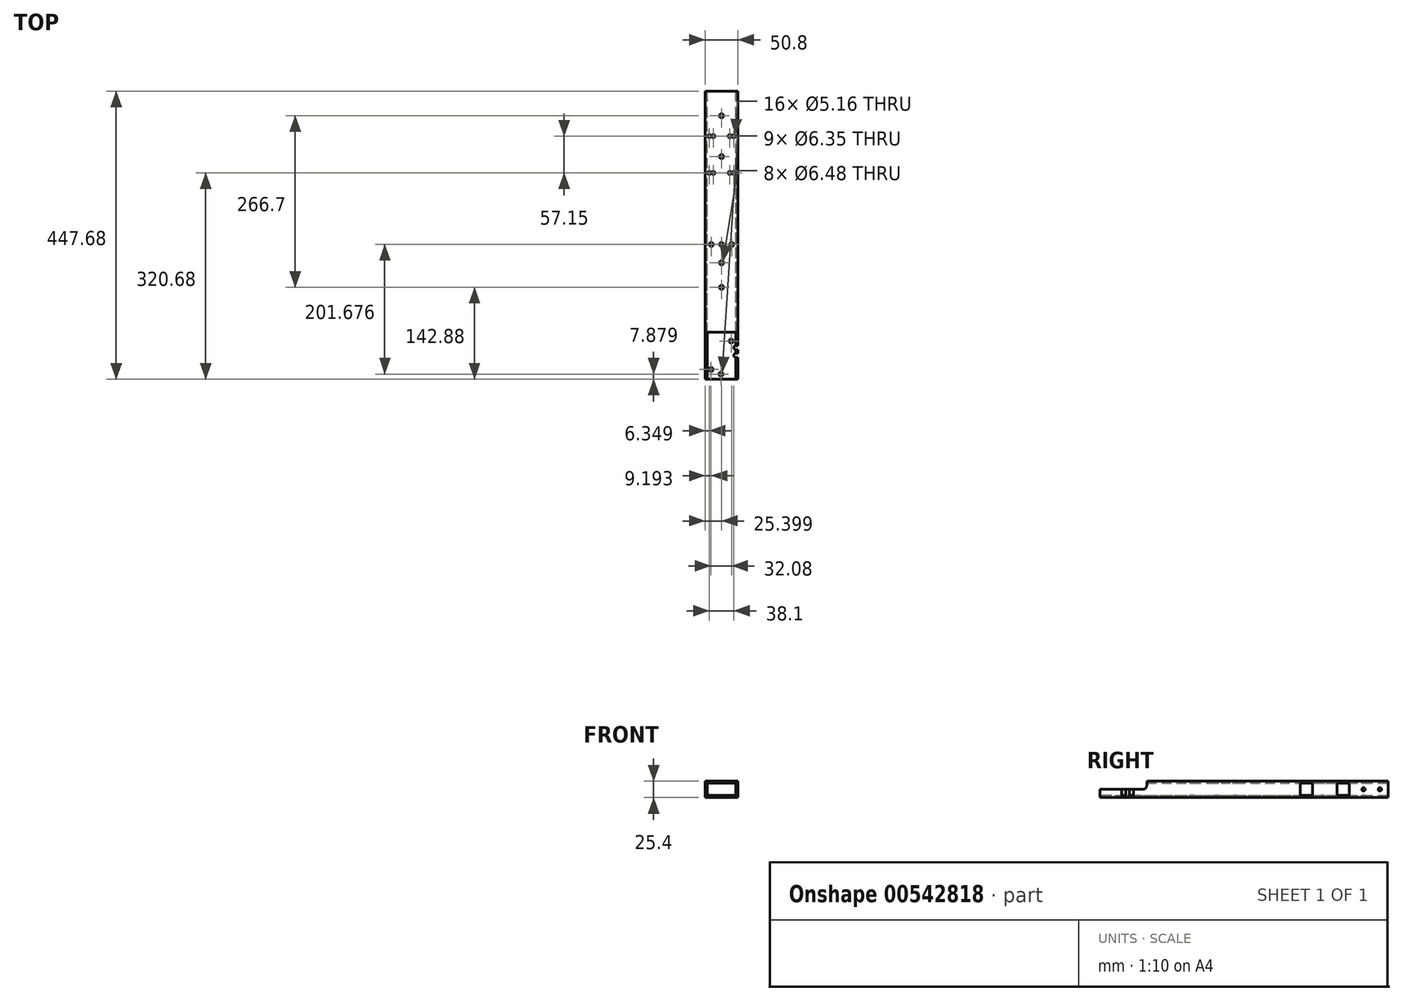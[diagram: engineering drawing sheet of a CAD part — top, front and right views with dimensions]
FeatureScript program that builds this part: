
annotation { "Feature Type Name" : "Feature", "Feature Type Description" : "" }
export const myFeature = defineFeature(function(context is Context, id is Id, definition is map)
    precondition{}
    {
        {
            var Q0;
            Q0=qCreatedBy(makeId("Front.planeOp"),FACE);
            var sketch = newSketch(context, id + "F0", { "sketchPlane" : qUnion([Q0])});
            skLineSegment(sketch, "E0.bottom", {"start": v(-52.6, 29.87) * mm, "end": v(-1.8, 29.87) * mm});
            skLineSegment(sketch, "E0.top", {"start": v(-52.6, 4.47) * mm, "end": v(-1.8, 4.47) * mm});
            skLineSegment(sketch, "E0.left", {"start": v(-52.6, 29.87) * mm, "end": v(-52.6, 4.47) * mm});
            skLineSegment(sketch, "E0.right", {"start": v(-1.8, 29.87) * mm, "end": v(-1.8, 4.47) * mm});
            skLineSegment(sketch, "E1.bottom", {"start": v(-49.43, 26.7) * mm, "end": v(-4.98, 26.7) * mm});
            skLineSegment(sketch, "E1.top", {"start": v(-49.43, 7.65) * mm, "end": v(-4.98, 7.65) * mm});
            skLineSegment(sketch, "E1.left", {"start": v(-49.43, 26.7) * mm, "end": v(-49.43, 7.65) * mm});
            skLineSegment(sketch, "E1.right", {"start": v(-4.98, 26.7) * mm, "end": v(-4.98, 7.65) * mm});
            skSolve(sketch);
        }
        {
            var Q0;
            Q0=makeQuery(id+"F0.imprint","IMPRINT",FACE,{"disambiguationData":[TD([[makeQuery(id+"F0.imprint","IMPRINT",EDGE,{"derivedFrom":sQuery(id+"F0.wireOp",EDGE,"E0.bottom")}),-1.0]])]});
            extrude(context, id + "F1", {"entities" : qUnion([Q0]), "depth" : 447.67 * mm, "offsetDistance" : 25.4 * mm});
        }
        {
            var Q0;
            Q0=makeQuery(id+"F1.opExtrude","SWEPT_FACE",FACE,{"disambiguationData":[OSD([sQuery(id+"F0.wireOp",EDGE,"E0.bottom")])]});
            var sketch = newSketch(context, id + "F2", { "sketchPlane" : qUnion([Q0])});
            skCircle(sketch, "E2", {"center": v(-27.2, -38.1) * mm, "radius": 3.24 * mm});
            skPoint(sketch, "E2.centerSnap0", {"position": v(-27.2, 0) * mm});
            skCircle(sketch, "E3", {"center": v(-27.2, -101.6) * mm, "radius": 3.24 * mm});
            skCircle(sketch, "E4", {"center": v(-27.2, -266.7) * mm, "radius": 3.24 * mm});
            skCircle(sketch, "E5", {"center": v(-27.2, -304.8) * mm, "radius": 3.24 * mm});
            skCircle(sketch, "E6", {"center": v(-46.25, -127) * mm, "radius": 2.58 * mm});
            skCircle(sketch, "E7", {"center": v(-39.9, -127) * mm, "radius": 2.58 * mm});
            skCircle(sketch, "E8", {"center": v(-14.5, -127) * mm, "radius": 2.58 * mm});
            skCircle(sketch, "E9", {"center": v(-8.15, -127) * mm, "radius": 2.58 * mm});
            skCircle(sketch, "E10", {"center": v(-46.25, -69.85) * mm, "radius": 2.58 * mm});
            skCircle(sketch, "E11", {"center": v(-39.9, -69.85) * mm, "radius": 2.58 * mm});
            skCircle(sketch, "E12", {"center": v(-14.5, -69.85) * mm, "radius": 2.58 * mm});
            skCircle(sketch, "E13", {"center": v(-8.15, -69.85) * mm, "radius": 2.58 * mm});
            skCircle(sketch, "E14", {"center": v(-43.08, -238.13) * mm, "radius": 3.18 * mm});
            skCircle(sketch, "E15", {"center": v(-27.2, -238.13) * mm, "radius": 3.18 * mm});
            skCircle(sketch, "E16", {"center": v(-11.33, -238.13) * mm, "radius": 3.18 * mm});
            skCircle(sketch, "E17", {"center": v(-12.09, -388.37) * mm, "radius": 3.18 * mm});
            skCircle(sketch, "E18", {"center": v(-27.96, -439.8) * mm, "radius": 3.18 * mm});
            skCircle(sketch, "E19", {"center": v(-43.4, -432.54) * mm, "radius": 3.18 * mm});
            skArc(sketch, "E20", {"start": v(-4.98, -407.54) * mm, "mid": v(-8.15, -410.72) * mm, "end": v(-4.98, -413.9) * mm});
            skArc(sketch, "E21", {"start": v(-4.98, -395.35) * mm, "mid": v(-8.15, -398.53) * mm, "end": v(-4.98, -401.7) * mm});
            skLineSegment(sketch, "E22", {"start": v(-4.98, -413.9) * mm, "end": v(-1.8, -413.9) * mm});
            skLineSegment(sketch, "E23", {"start": v(-4.98, -407.54) * mm, "end": v(-1.8, -407.54) * mm});
            skLineSegment(sketch, "E24", {"start": v(-4.98, -401.7) * mm, "end": v(-1.8, -401.7) * mm});
            skLineSegment(sketch, "E25", {"start": v(-4.98, -395.35) * mm, "end": v(-1.8, -395.35) * mm});
            skSolve(sketch);
        }
        {
            var Q0;
            Q0=makeQuery(id+"F2.imprint","IMPRINT",FACE,{"disambiguationData":[TD([[makeQuery(id+"F2.imprint","IMPRINT",EDGE,{"derivedFrom":sQuery(id+"F2.wireOp",EDGE,"E5")}),1.0]])]});
            var Q1;
            Q1=makeQuery(id+"F2.imprint","IMPRINT",FACE,{"disambiguationData":[TD([[makeQuery(id+"F2.imprint","IMPRINT",EDGE,{"derivedFrom":sQuery(id+"F2.wireOp",EDGE,"E4")}),1.0]])]});
            var Q2;
            Q2=makeQuery(id+"F2.imprint","IMPRINT",FACE,{"disambiguationData":[TD([[makeQuery(id+"F2.imprint","IMPRINT",EDGE,{"derivedFrom":sQuery(id+"F2.wireOp",EDGE,"E3")}),1.0]])]});
            var Q3;
            Q3=makeQuery(id+"F2.imprint","IMPRINT",FACE,{"disambiguationData":[TD([[makeQuery(id+"F2.imprint","IMPRINT",EDGE,{"derivedFrom":sQuery(id+"F2.wireOp",EDGE,"E2")}),1.0]])]});
            var Q4;
            Q4=makeQuery(id+"F2.imprint","IMPRINT",FACE,{"disambiguationData":[TD([[makeQuery(id+"F2.imprint","IMPRINT",EDGE,{"derivedFrom":sQuery(id+"F2.wireOp",EDGE,"E6")}),1.0]])]});
            var Q5;
            Q5=makeQuery(id+"F2.imprint","IMPRINT",FACE,{"disambiguationData":[TD([[makeQuery(id+"F2.imprint","IMPRINT",EDGE,{"derivedFrom":sQuery(id+"F2.wireOp",EDGE,"E7")}),1.0]])]});
            var Q6;
            Q6=makeQuery(id+"F2.imprint","IMPRINT",FACE,{"disambiguationData":[TD([[makeQuery(id+"F2.imprint","IMPRINT",EDGE,{"derivedFrom":sQuery(id+"F2.wireOp",EDGE,"E8")}),1.0]])]});
            var Q7;
            Q7=makeQuery(id+"F2.imprint","IMPRINT",FACE,{"disambiguationData":[TD([[makeQuery(id+"F2.imprint","IMPRINT",EDGE,{"derivedFrom":sQuery(id+"F2.wireOp",EDGE,"E9")}),1.0]])]});
            var Q8;
            Q8=makeQuery(id+"F2.imprint","IMPRINT",FACE,{"disambiguationData":[TD([[makeQuery(id+"F2.imprint","IMPRINT",EDGE,{"derivedFrom":sQuery(id+"F2.wireOp",EDGE,"E10")}),1.0]])]});
            var Q9;
            Q9=makeQuery(id+"F2.imprint","IMPRINT",FACE,{"disambiguationData":[TD([[makeQuery(id+"F2.imprint","IMPRINT",EDGE,{"derivedFrom":sQuery(id+"F2.wireOp",EDGE,"E11")}),1.0]])]});
            var Q10;
            Q10=makeQuery(id+"F2.imprint","IMPRINT",FACE,{"disambiguationData":[TD([[makeQuery(id+"F2.imprint","IMPRINT",EDGE,{"derivedFrom":sQuery(id+"F2.wireOp",EDGE,"E12")}),1.0]])]});
            var Q11;
            Q11=makeQuery(id+"F2.imprint","IMPRINT",FACE,{"disambiguationData":[TD([[makeQuery(id+"F2.imprint","IMPRINT",EDGE,{"derivedFrom":sQuery(id+"F2.wireOp",EDGE,"E13")}),1.0]])]});
            var Q12;
            Q12=makeQuery(id+"F2.imprint","IMPRINT",FACE,{"disambiguationData":[TD([[makeQuery(id+"F2.imprint","IMPRINT",EDGE,{"derivedFrom":sQuery(id+"F2.wireOp",EDGE,"E14")}),1.0]])]});
            var Q13;
            Q13=makeQuery(id+"F2.imprint","IMPRINT",FACE,{"disambiguationData":[TD([[makeQuery(id+"F2.imprint","IMPRINT",EDGE,{"derivedFrom":sQuery(id+"F2.wireOp",EDGE,"E15")}),1.0]])]});
            var Q14;
            Q14=makeQuery(id+"F2.imprint","IMPRINT",FACE,{"disambiguationData":[TD([[makeQuery(id+"F2.imprint","IMPRINT",EDGE,{"derivedFrom":sQuery(id+"F2.wireOp",EDGE,"E16")}),1.0]])]});
            var Q15;
            Q15=makeQuery(id+"F2.imprint","IMPRINT",FACE,{"disambiguationData":[TD([[makeQuery(id+"F2.imprint","IMPRINT",EDGE,{"derivedFrom":sQuery(id+"F2.wireOp",EDGE,"E17")}),1.0]])]});
            extrude(context, id + "F3", {"entities" : qUnion([Q0, Q1, Q2, Q3, Q4, Q5, Q6, Q7, Q8, Q9, Q10, Q11, Q12, Q13, Q14, Q15]), "operationType" : NewBodyOperationType.REMOVE, "oppositeDirection" : true, "depth" : 25.4 * mm, "offsetDistance" : 25.4 * mm});
        }
        {
            var Q0;
            Q0=makeQuery(id+"F1.opExtrude","SWEPT_FACE",FACE,{"disambiguationData":[OSD([sQuery(id+"F0.wireOp",EDGE,"E0.left")])]});
            var sketch = newSketch(context, id + "F4", { "sketchPlane" : qUnion([Q0])});
            skCircle(sketch, "E26", {"center": v(12.7, 17.17) * mm, "radius": 2.58 * mm});
            skPoint(sketch, "E26.centerSnap0", {"position": v(0, 17.17) * mm});
            skCircle(sketch, "E27", {"center": v(38.1, 17.17) * mm, "radius": 2.58 * mm});
            skLineSegment(sketch, "E28.bottom", {"start": v(61.93, 7.65) * mm, "end": v(77.77, 7.65) * mm});
            skLineSegment(sketch, "E28.top", {"start": v(61.93, 26.7) * mm, "end": v(77.77, 26.7) * mm});
            skLineSegment(sketch, "E28.left", {"start": v(60.33, 9.25) * mm, "end": v(60.33, 25.1) * mm});
            skLineSegment(sketch, "E28.right", {"start": v(79.38, 9.25) * mm, "end": v(79.38, 25.1) * mm});
            skArc(sketch, "E29", {"start": v(61.93, 7.65) * mm, "mid": v(60.8, 8.12) * mm, "end": v(60.33, 9.25) * mm});
            skArc(sketch, "E30", {"start": v(60.33, 25.1) * mm, "mid": v(60.8, 26.23) * mm, "end": v(61.93, 26.7) * mm});
            skArc(sketch, "E31", {"start": v(77.77, 26.7) * mm, "mid": v(78.9, 26.23) * mm, "end": v(79.38, 25.1) * mm});
            skArc(sketch, "E32", {"start": v(79.38, 9.25) * mm, "mid": v(78.9, 8.12) * mm, "end": v(77.77, 7.65) * mm});
            skLineSegment(sketch, "E33.bottom", {"start": v(119.08, 7.65) * mm, "end": v(134.92, 7.65) * mm});
            skLineSegment(sketch, "E33.top", {"start": v(119.08, 26.7) * mm, "end": v(134.92, 26.7) * mm});
            skLineSegment(sketch, "E33.left", {"start": v(117.47, 9.25) * mm, "end": v(117.47, 25.1) * mm});
            skLineSegment(sketch, "E33.right", {"start": v(136.53, 9.25) * mm, "end": v(136.53, 25.1) * mm});
            skArc(sketch, "E34", {"start": v(119.08, 7.65) * mm, "mid": v(117.94, 8.12) * mm, "end": v(117.47, 9.25) * mm});
            skArc(sketch, "E35", {"start": v(117.47, 25.1) * mm, "mid": v(117.94, 26.23) * mm, "end": v(119.08, 26.7) * mm});
            skArc(sketch, "E36", {"start": v(134.92, 26.7) * mm, "mid": v(136.06, 26.23) * mm, "end": v(136.53, 25.1) * mm});
            skArc(sketch, "E37", {"start": v(136.53, 9.25) * mm, "mid": v(136.06, 8.12) * mm, "end": v(134.92, 7.65) * mm});
            skLineSegment(sketch, "E38.bottom", {"start": v(381, 17.17) * mm, "end": v(447.68, 17.17) * mm});
            skLineSegment(sketch, "E38.top", {"start": v(374.65, 29.87) * mm, "end": v(447.68, 29.87) * mm});
            skLineSegment(sketch, "E38.left", {"start": v(374.65, 23.52) * mm, "end": v(374.65, 29.87) * mm});
            skLineSegment(sketch, "E38.right", {"start": v(447.68, 17.17) * mm, "end": v(447.68, 29.87) * mm});
            skArc(sketch, "E39", {"start": v(381, 17.17) * mm, "mid": v(376.5, 19.03) * mm, "end": v(374.65, 23.52) * mm});
            skSolve(sketch);
        }
        {
            var Q0;
            Q0=makeQuery(id+"F4.imprint","IMPRINT",FACE,{"disambiguationData":[TD([[makeQuery(id+"F4.imprint","IMPRINT",EDGE,{"derivedFrom":sQuery(id+"F4.wireOp",EDGE,"E27")}),1.0]])]});
            var Q1;
            Q1=makeQuery(id+"F4.imprint","IMPRINT",FACE,{"disambiguationData":[TD([[makeQuery(id+"F4.imprint","IMPRINT",EDGE,{"derivedFrom":sQuery(id+"F4.wireOp",EDGE,"E26")}),1.0]])]});
            var Q2;
            Q2=makeQuery(id+"F4.imprint","IMPRINT",FACE,{"disambiguationData":[TD([[makeQuery(id+"F4.imprint","IMPRINT",EDGE,{"derivedFrom":sQuery(id+"F4.wireOp",EDGE,"E28.bottom")}),1.0]])]});
            var Q3;
            Q3=makeQuery(id+"F4.imprint","IMPRINT",FACE,{"disambiguationData":[TD([[makeQuery(id+"F4.imprint","IMPRINT",EDGE,{"derivedFrom":sQuery(id+"F4.wireOp",EDGE,"E33.bottom")}),1.0]])]});
            extrude(context, id + "F5", {"entities" : qUnion([Q0, Q1, Q2, Q3]), "operationType" : NewBodyOperationType.REMOVE, "endBound" : BoundingType.THROUGH_ALL, "oppositeDirection" : true, "depth" : 25.4 * mm, "offsetDistance" : 25.4 * mm});
        }
        {
            var Q0;
            Q0=qSketchRegion(id+"F4",true);
            extrude(context, id + "F6", {"entities" : qUnion([Q0]), "operationType" : NewBodyOperationType.REMOVE, "oppositeDirection" : true, "depth" : 76.2 * mm, "offsetDistance" : 25.4 * mm});
        }
        {
            var Q0;
            Q0=makeQuery(id+"F2.imprint","IMPRINT",FACE,{"disambiguationData":[TD([[makeQuery(id+"F2.imprint","IMPRINT",EDGE,{"derivedFrom":sQuery(id+"F2.wireOp",EDGE,"E18")}),1.0]])]});
            var Q1;
            Q1=makeQuery(id+"F2.imprint","IMPRINT",FACE,{"disambiguationData":[TD([[makeQuery(id+"F2.imprint","IMPRINT",EDGE,{"derivedFrom":sQuery(id+"F2.wireOp",EDGE,"E19")}),1.0]])]});
            var Q2;
            Q2=makeQuery(id+"F2.imprint","IMPRINT",FACE,{"disambiguationData":[TD([[makeQuery(id+"F2.imprint","IMPRINT",EDGE,{"derivedFrom":sQuery(id+"F2.wireOp",EDGE,"E20")}),1.0]])]});
            var Q3;
            Q3=makeQuery(id+"F2.imprint","IMPRINT",FACE,{"disambiguationData":[TD([[makeQuery(id+"F2.imprint","IMPRINT",EDGE,{"derivedFrom":sQuery(id+"F2.wireOp",EDGE,"E21")}),1.0]])]});
            extrude(context, id + "F7", {"entities" : qUnion([Q0, Q1, Q2, Q3]), "operationType" : NewBodyOperationType.REMOVE, "oppositeDirection" : true, "depth" : 25.4 * mm, "offsetDistance" : 25.4 * mm});
        }
    });
